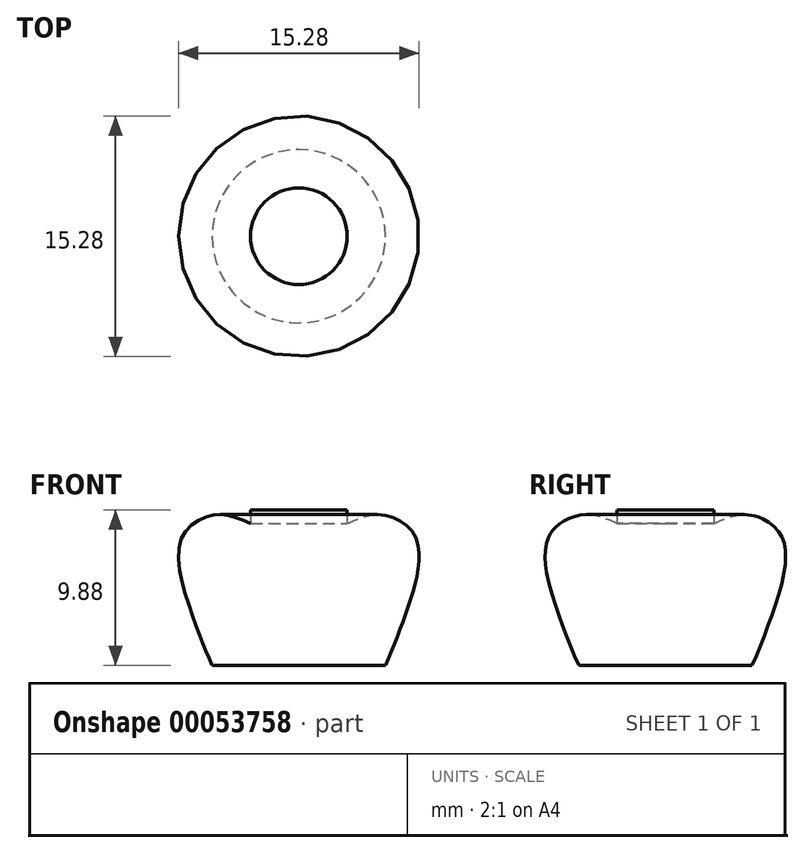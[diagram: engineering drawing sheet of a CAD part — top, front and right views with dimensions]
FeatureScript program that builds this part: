
annotation { "Feature Type Name" : "Feature", "Feature Type Description" : "" }
export const myFeature = defineFeature(function(context is Context, id is Id, definition is map)
    precondition{}
    {
        {
            var Q0;
            Q0=qCreatedBy(makeId("Front.planeOp"),FACE);
            var sketch = newSketch(context, id + "F0", { "sketchPlane" : qUnion([Q0])});
            skLineSegment(sketch, "E0", {"start": v(0, 0) * mm, "end": v(-5.5, 0) * mm});
            skLineSegment(sketch, "E1", {"start": v(0, 9.88) * mm, "end": v(-3.07, 9.88) * mm});
            skLineSegment(sketch, "E2", {"start": v(-3.07, 9.88) * mm, "end": v(-3.07, 9.02) * mm});
            skFitSpline(sketch, "E3", {"points": [v(-5.5, 0) * mm, v(-6.68, 2.96) * mm, v(-7.49, 7.97) * mm, v(-5.35, 9.57) * mm, v(-3.07, 9.02) * mm], "startDerivative": vector(-5.07, 10.95) * mm, "endDerivative": vector(12.38, -5.5) * mm});
            skLineSegment(sketch, "E4", {"start": v(0, 9.88) * mm, "end": v(0, 0) * mm});
            skLineSegment(sketch, "E5", {"start": v(0, 0) * mm, "end": v(0, 18.5) * mm});
            skSolve(sketch);
        }
        {
            var Q0;
            Q0 = qSketchRegion(id + "F0", true);
            var Q1;
            Q1=sQuery(id+"F0.wireOp",EDGE,"E5");
            revolve(context, id + "F1", {"entities" : qUnion([Q0]), "axis" : qUnion([Q1]), "revolveType" : RevolveType.FULL});
        }
    });
